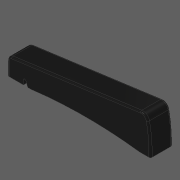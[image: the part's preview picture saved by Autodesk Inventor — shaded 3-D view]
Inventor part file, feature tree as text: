
AUTODESK INVENTOR PART (.ipt)
format: ipt  version: 2020 (Build 240168000, 168)  size: 276,480 bytes
history: native  units: in
note: dims shown in document units (in); Inventor stores cm internally (conversion verified against a paired STEP export)
features: other x3, extrude x3, fillet x2
ambient origin geometry x8: Origin, YZ Plane, XZ Plane, XY Plane, X Axis, Y Axis, Z Axis, Center Point
bodies: Solid1 (feature_tree)
feature tree (8):
  other  "Slot Start Plane"
  other  "Key Profile"
  extrude  "Key"  Depth=0.0787in
  extrude  "Protrusion Cutout"  TaperAngle=0.0deg  [1 undecoded]
  fillet  "Front Fillet"  [1 undecoded]
  extrude  "Slot"  Depth=0.1181in
  fillet  "Edge Softening"  Radius=0.1374in
  other  "Slot Sketch"
note: 2 required parameter values undecoded (feature->parameter linkage not recoverable at this tier; creation-order binding heuristic only, values carry confidence <= 0.55)
